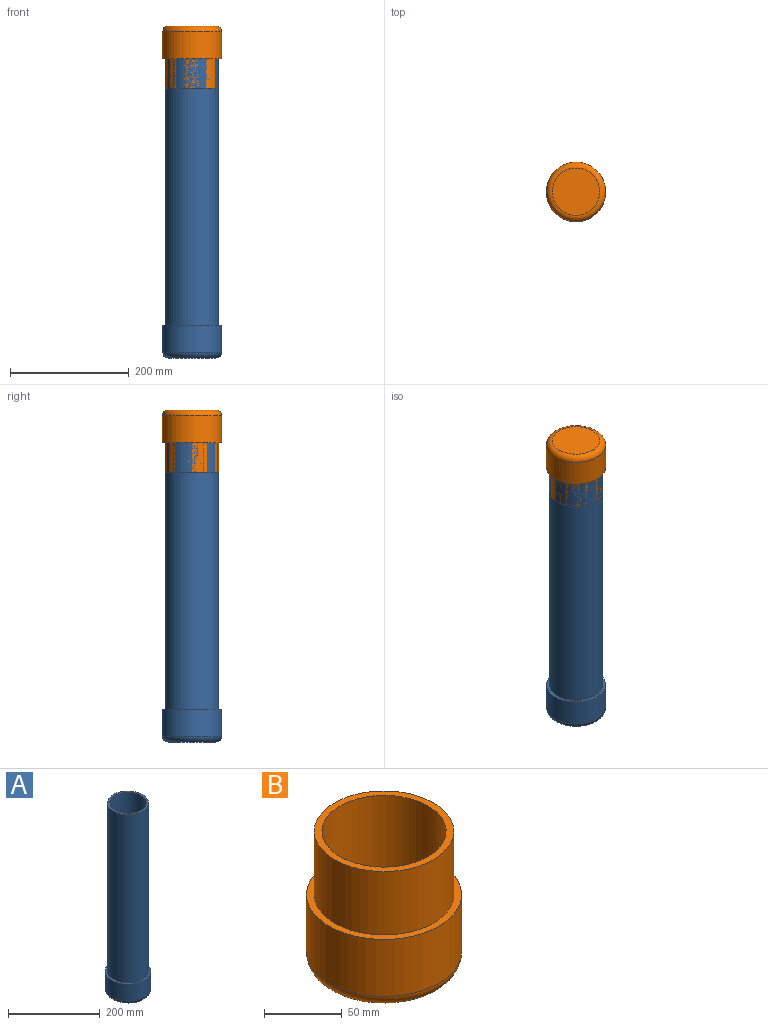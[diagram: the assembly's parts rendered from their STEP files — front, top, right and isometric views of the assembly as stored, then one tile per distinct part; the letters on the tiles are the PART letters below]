
ASSEMBLY  parts=2 mates=1
PART A: 8 faces, bbox 108.2x108.2x505 mm
  f0: cylinder r=50mm len=100mm, axis (0,0,-1), area 14137.2mm2, adj f1,f7
  f1: plane 100x100mm, normal (0,0,1), area 1492.3mm2, adj f0,f2
  f2: cylinder r=45mm len=450mm, axis (0,0,-1), area 127234.5mm2, adj f1,f4
  f3: cylinder r=40mm len=500mm, axis (0,0,-1), area 125663.7mm2, adj f4,f5
  f4: plane 90x90mm, normal (0,0,1), area 1335.2mm2, adj f2,f3
  f5: plane 80x80mm, normal (0,0,1), area 5026.5mm2, adj f3
  f6: plane 80x80mm, normal (0,0,-1), area 5026.5mm2, adj f7
  f7: torus R=40mm, axis (0,0,1), area 4576.2mm2, adj f0,f6
PART B: 8 faces, bbox 108.2x108.2x105 mm
  f0: cylinder r=50mm len=100mm, axis (0,0,-1), area 14137.2mm2, adj f1,f7
  f1: plane 100x100mm, normal (0,0,1), area 1492.3mm2, adj f0,f2
  f2: cylinder r=45mm len=90mm, axis (0,0,-1), area 14137.2mm2, adj f1,f4
  f3: cylinder r=40mm len=100mm, axis (0,0,-1), area 25132.7mm2, adj f4,f5
  f4: plane 90x90mm, normal (0,0,1), area 1335.2mm2, adj f2,f3
  f5: plane 80x80mm, normal (0,0,1), area 5026.5mm2, adj f3
  f6: plane 80x80mm, normal (0,0,-1), area 5026.5mm2, adj f7
  f7: torus R=40mm, axis (0,0,1), area 4576.2mm2, adj f0,f6
PLACE A t=(-20.39,11.86,-212.06)mm
PLACE B rot(axis=(1,0,0),180deg) t=(-20.39,11.86,337.94)mm
MATE pin_slot B.f0 <-> A.f0  axis (0,0,1) through (-20.39,11.86,287.94)mm
